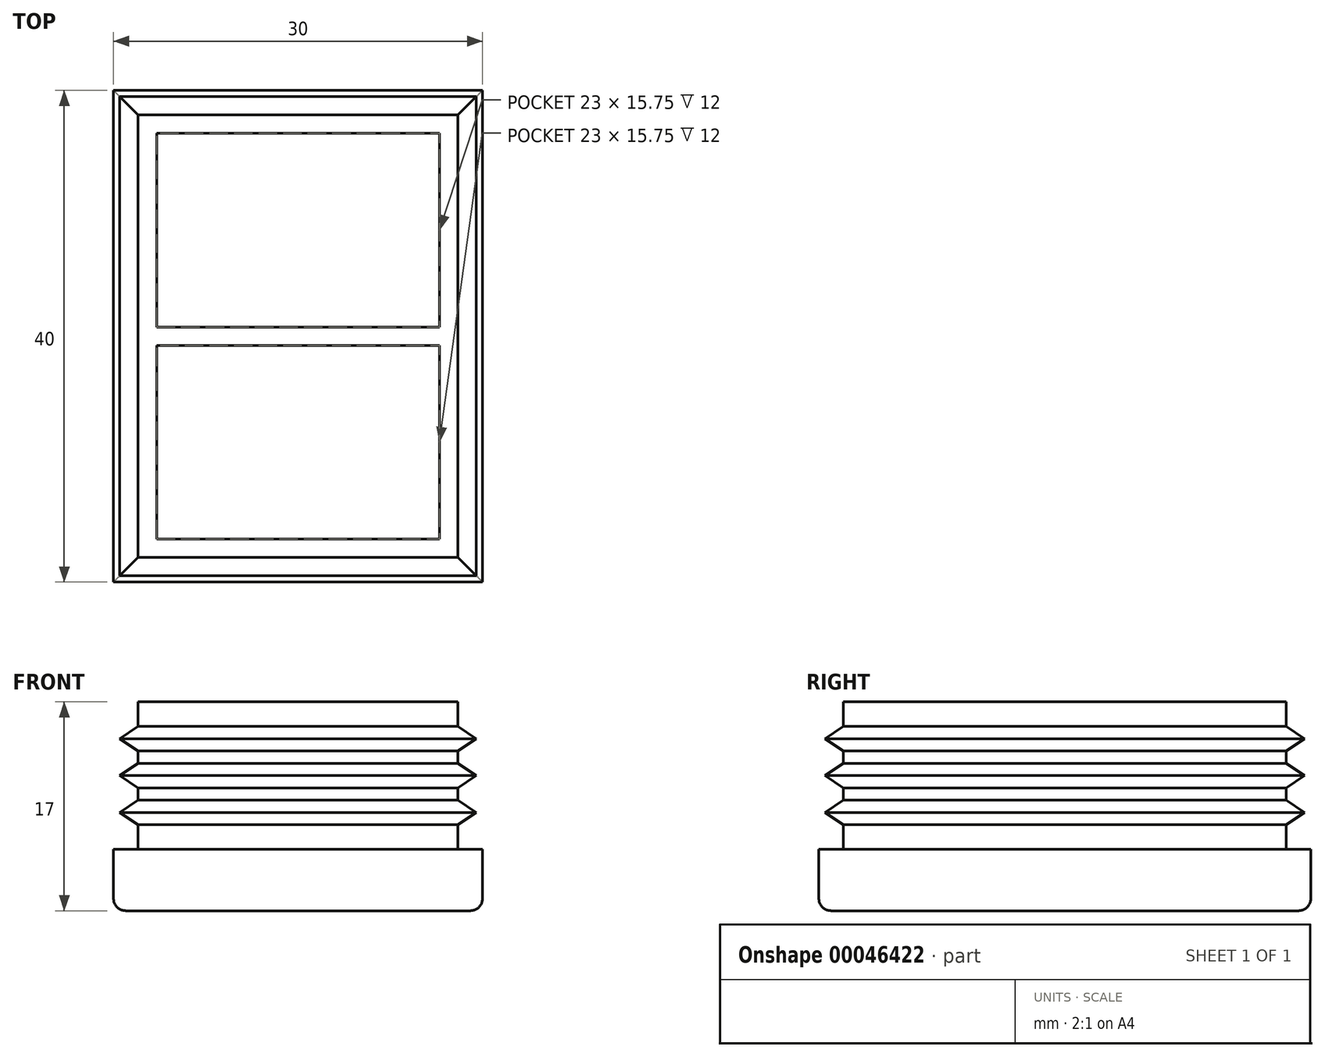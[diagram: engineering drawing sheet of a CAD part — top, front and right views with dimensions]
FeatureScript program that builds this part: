
annotation { "Feature Type Name" : "Feature", "Feature Type Description" : "" }
export const myFeature = defineFeature(function(context is Context, id is Id, definition is map)
    precondition{}
    {
        {
            var Q0;
            Q0=qCreatedBy(makeId("Top.planeOp"),FACE);
            var sketch = newSketch(context, id + "F0", { "sketchPlane" : qUnion([Q0])});
            skLineSegment(sketch, "E0.bottom", {"start": v(15, -20) * mm, "end": v(-15, -20) * mm});
            skLineSegment(sketch, "E0.top", {"start": v(15, 20) * mm, "end": v(-15, 20) * mm});
            skLineSegment(sketch, "E0.left", {"start": v(15, -20) * mm, "end": v(15, 20) * mm});
            skLineSegment(sketch, "E0.right", {"start": v(-15, -20) * mm, "end": v(-15, 20) * mm});
            skPoint(sketch, "E0.middle", {"position": v(0, 0) * mm});
            skSolve(sketch);
        }
        {
            var Q0;
            Q0=makeQuery(id+"F0.imprint","IMPRINT",FACE,{"disambiguationData":[TD([[makeQuery(id+"F0.imprint","IMPRINT",EDGE,{"derivedFrom":sQuery(id+"F0.wireOp",EDGE,"E0.bottom")}),-1.0]])]});
            extrude(context, id + "F1", {"entities" : qUnion([Q0]), "depth" : 5 * mm, "offsetDistance" : 25 * mm});
        }
        {
            var Q0;
            Q0=makeQuery(id+"F1.opExtrude","CAP_EDGE",EDGE,{"disambiguationData":[OSD([sQuery(id+"F0.wireOp",EDGE,"E0.bottom")])],"isStart":true});
            var Q1;
            Q1=makeQuery(id+"F1.opExtrude","CAP_EDGE",EDGE,{"disambiguationData":[OSD([sQuery(id+"F0.wireOp",EDGE,"E0.left")])],"isStart":true});
            var Q2;
            Q2=makeQuery(id+"F1.opExtrude","CAP_EDGE",EDGE,{"disambiguationData":[OSD([sQuery(id+"F0.wireOp",EDGE,"E0.top")])],"isStart":true});
            var Q3;
            Q3=makeQuery(id+"F1.opExtrude","CAP_EDGE",EDGE,{"disambiguationData":[OSD([sQuery(id+"F0.wireOp",EDGE,"E0.right")])],"isStart":true});
            fillet(context, id + "F2", {"entities" : qUnion([Q0, Q1, Q2, Q3]), "tangentPropagation" : true, "radius" : 1 * mm, "defaultsChanged" : false, "vertexSettings" : [], "allowEdgeOverflow" : false});
        }
        {
            var Q0;
            Q0=makeQuery(id+"F1.opExtrude","CAP_FACE",FACE,{"disambiguationData":[OSD([sQuery(id+"F0.wireOp",EDGE,"E0.bottom"),sQuery(id+"F0.wireOp",EDGE,"E0.top"),sQuery(id+"F0.wireOp",EDGE,"E0.left"),sQuery(id+"F0.wireOp",EDGE,"E0.right")])],"isStart":false});
            var sketch = newSketch(context, id + "F3", { "sketchPlane" : qUnion([Q0])});
            skLineSegment(sketch, "E1.bottom", {"start": v(11.5, 16.5) * mm, "end": v(-11.5, 16.5) * mm});
            skLineSegment(sketch, "E1.top", {"start": v(11.5, -16.5) * mm, "end": v(-11.5, -16.5) * mm});
            skLineSegment(sketch, "E1.left", {"start": v(11.5, 16.5) * mm, "end": v(11.5, -16.5) * mm});
            skLineSegment(sketch, "E1.right", {"start": v(-11.5, 16.5) * mm, "end": v(-11.5, -16.5) * mm});
            skPoint(sketch, "E1.middle", {"position": v(0, 0) * mm});
            skLineSegment(sketch, "E2.0", {"start": v(20, -25) * mm, "end": v(20, 25) * mm});
            skLineSegment(sketch, "E2.1", {"start": v(-20, -25) * mm, "end": v(20, -25) * mm});
            skLineSegment(sketch, "E2.2", {"start": v(-20, 25) * mm, "end": v(-20, -25) * mm});
            skLineSegment(sketch, "E2.3", {"start": v(20, 25) * mm, "end": v(-20, 25) * mm});
            skLineSegment(sketch, "E3.0", {"start": v(13, -18) * mm, "end": v(-13, -18) * mm});
            skLineSegment(sketch, "E3.1", {"start": v(13, 18) * mm, "end": v(13, -18) * mm});
            skLineSegment(sketch, "E3.2", {"start": v(13, 18) * mm, "end": v(-13, 18) * mm});
            skLineSegment(sketch, "E3.3", {"start": v(-13, 18) * mm, "end": v(-13, -18) * mm});
            skLineSegment(sketch, "E4.bottom", {"start": v(11.5, -0.75) * mm, "end": v(-11.5, -0.75) * mm});
            skLineSegment(sketch, "E4.top", {"start": v(11.5, 0.75) * mm, "end": v(-11.5, 0.75) * mm});
            skLineSegment(sketch, "E4.left", {"start": v(11.5, -0.75) * mm, "end": v(11.5, 0.75) * mm});
            skLineSegment(sketch, "E4.right", {"start": v(-11.5, -0.75) * mm, "end": v(-11.5, 0.75) * mm});
            skSolve(sketch);
        }
        {
            var Q0;
            {var subQ5=sQuery(id+"F3.wireOp",EDGE,"E1.bottom");Q0=makeQuery(id+"F3.imprint","IMPRINT",FACE,{"disambiguationData":[TD([[makeQuery(id+"F3.imprint","IMPRINT",EDGE,{"derivedFrom":subQ5}),-1.0]])]});}
            var Q1;
            {var subQ0=sQuery(id+"F3.wireOp",EDGE,"E4.bottom");Q1=makeQuery(id+"F3.imprint","IMPRINT",FACE,{"disambiguationData":[TD([[makeQuery(id+"F3.imprint","IMPRINT",EDGE,{"derivedFrom":subQ0}),-1.0]])]});}
            extrude(context, id + "F4", {"entities" : qUnion([Q0, Q1]), "operationType" : NewBodyOperationType.ADD, "depth" : 12 * mm, "offsetDistance" : 25 * mm});
        }
        {
            var Q0;
            Q0=makeQuery(id+"F4.opExtrude","SWEPT_FACE",FACE,{"disambiguationData":[OSD([sQuery(id+"F3.wireOp",EDGE,"E3.0")])]});
            var sketch = newSketch(context, id + "F5", { "sketchPlane" : qUnion([Q0])});
            skPoint(sketch, "E5", {"position": v(-13, 8) * mm});
            skLineSegment(sketch, "E6", {"start": v(-13, 7) * mm, "end": v(-14.5, 8) * mm});
            skLineSegment(sketch, "E7", {"start": v(-14.5, 8) * mm, "end": v(-13, 9) * mm});
            skPoint(sketch, "E8.0.1.0", {"position": v(-13, 11) * mm});
            skLineSegment(sketch, "E8.0.1.1", {"start": v(-13, 10) * mm, "end": v(-14.5, 11) * mm});
            skLineSegment(sketch, "E8.0.1.2", {"start": v(-14.5, 11) * mm, "end": v(-13, 12) * mm});
            skPoint(sketch, "E8.0.2.0", {"position": v(-13, 14) * mm});
            skLineSegment(sketch, "E8.0.2.1", {"start": v(-13, 13) * mm, "end": v(-14.5, 14) * mm});
            skLineSegment(sketch, "E8.0.2.2", {"start": v(-14.5, 14) * mm, "end": v(-13, 15) * mm});
            skLineSegment(sketch, "E8.direction1", {"start": v(-14.5, 8) * mm, "end": v(10.5, 8) * mm, "construction": true});
            skLineSegment(sketch, "E8.direction2", {"start": v(-14.5, 8) * mm, "end": v(-14.5, 11) * mm, "construction": true});
            skSolve(sketch);
        }
        {
            var Q0;
            {var subQ0=sQuery(id+"F5.wireOp",EDGE,"E6");Q0=makeQuery(id+"F5.imprint","IMPRINT",FACE,{"disambiguationData":[TD([[makeQuery(id+"F5.imprint","IMPRINT",EDGE,{"derivedFrom":subQ0}),-1.0]])]});}
            var Q1;
            {var subQ0=sQuery(id+"F5.wireOp",EDGE,"E8.0.1.1");Q1=makeQuery(id+"F5.imprint","IMPRINT",FACE,{"disambiguationData":[TD([[makeQuery(id+"F5.imprint","IMPRINT",EDGE,{"derivedFrom":subQ0}),-1.0]])]});}
            var Q2;
            {var subQ0=sQuery(id+"F5.wireOp",EDGE,"E8.0.2.1");Q2=makeQuery(id+"F5.imprint","IMPRINT",FACE,{"disambiguationData":[TD([[makeQuery(id+"F5.imprint","IMPRINT",EDGE,{"derivedFrom":subQ0}),-1.0]])]});}
            var Q3;
            Q3=makeQuery(id+"F4.opExtrude","CAP_EDGE",EDGE,{"disambiguationData":[OSD([sQuery(id+"F3.wireOp",EDGE,"E3.3")])],"isStart":false});
            var Q4;
            Q4=makeQuery(id+"F4.opExtrude","CAP_EDGE",EDGE,{"disambiguationData":[OSD([sQuery(id+"F3.wireOp",EDGE,"E3.2")])],"isStart":false});
            var Q5;
            Q5=makeQuery(id+"F4.opExtrude","CAP_EDGE",EDGE,{"disambiguationData":[OSD([sQuery(id+"F3.wireOp",EDGE,"E3.1")])],"isStart":false});
            var Q6;
            Q6=makeQuery(id+"F4.opExtrude","CAP_EDGE",EDGE,{"disambiguationData":[OSD([sQuery(id+"F3.wireOp",EDGE,"E3.0")])],"isStart":false});
            sweep(context, id + "F6", {"operationType" : NewBodyOperationType.ADD, "profiles" : qUnion([Q0, Q1, Q2]), "path" : qUnion([Q3, Q4, Q5, Q6])});
        }
    });
